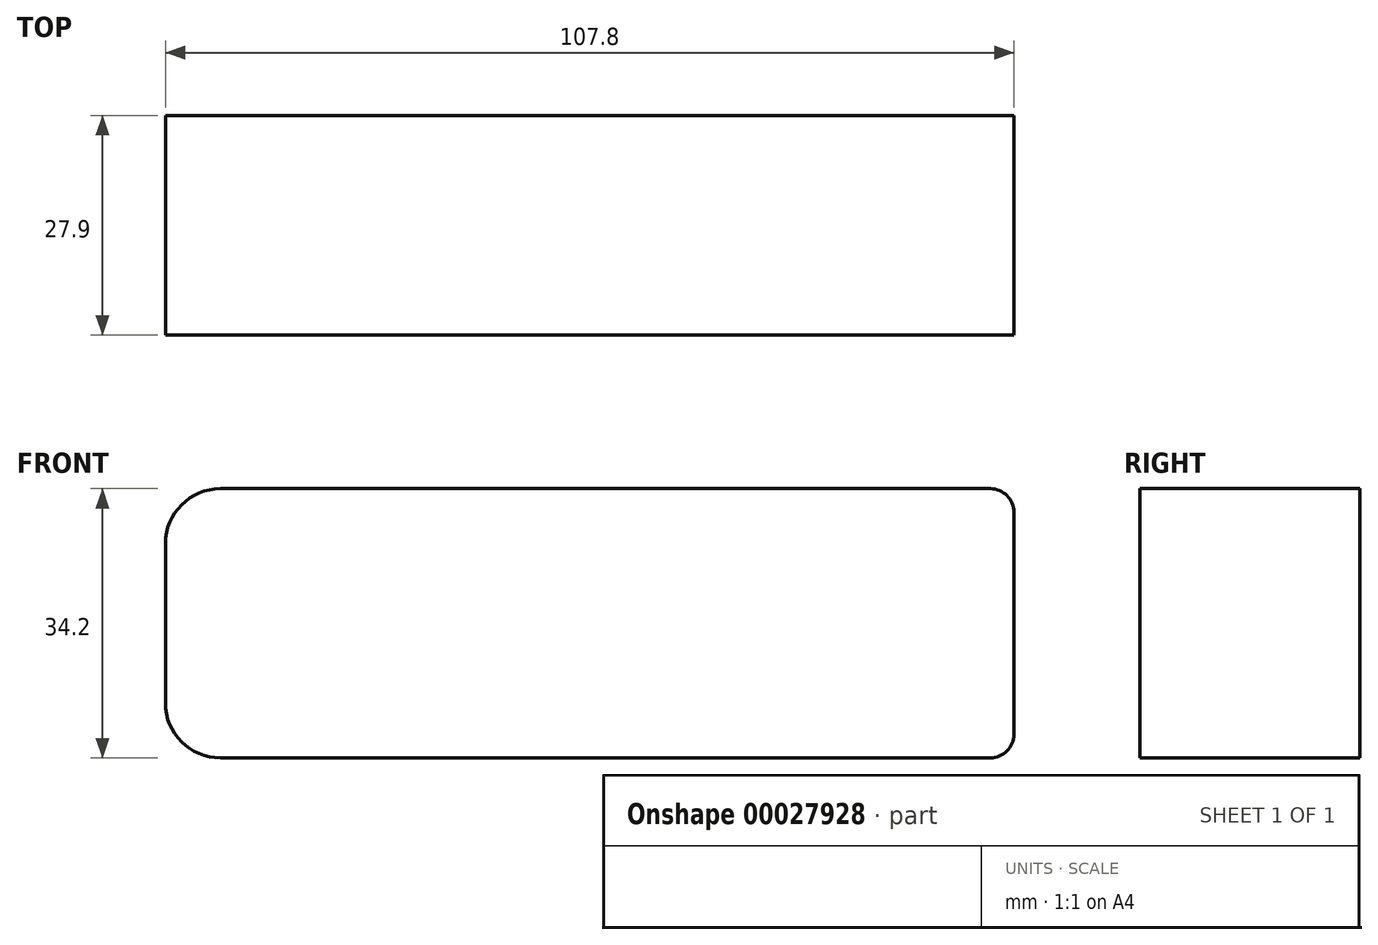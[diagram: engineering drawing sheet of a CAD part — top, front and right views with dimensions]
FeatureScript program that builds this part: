
annotation { "Feature Type Name" : "Feature", "Feature Type Description" : "" }
export const myFeature = defineFeature(function(context is Context, id is Id, definition is map)
    precondition{}
    {
        {
            var Q0;
            Q0=qCreatedBy(makeId("Top.planeOp"),FACE);
            var sketch = newSketch(context, id + "F0", { "sketchPlane" : qUnion([Q0])});
            skLineSegment(sketch, "E0.rect.bottom", {"start": v(53.9, -13.95) * mm, "end": v(-53.9, -13.95) * mm});
            skLineSegment(sketch, "E0.rect.top", {"start": v(53.9, 13.95) * mm, "end": v(-53.9, 13.95) * mm});
            skLineSegment(sketch, "E0.rect.left", {"start": v(53.9, -13.95) * mm, "end": v(53.9, 13.95) * mm});
            skLineSegment(sketch, "E0.rect.right", {"start": v(-53.9, -13.95) * mm, "end": v(-53.9, 13.95) * mm});
            skPoint(sketch, "E0.rect.middle", {"position": v(0, 0) * mm});
            skSolve(sketch);
        }
        {
            var Q0;
            Q0 = qSketchRegion(id + "F0", true);
            extrude(context, id + "F1", {"entities" : qUnion([Q0]), "depth" : 34.2 * mm});
        }
        {
            var Q0;
            Q0=makeQuery(id+"F1.opExtrude","CAP_EDGE",EDGE,{"disambiguationData":[OSD([sQuery(id+"F0.wireOp",EDGE,"E0.rect.right")])],"isStart":false});
            var Q1;
            Q1=makeQuery(id+"F1.opExtrude","CAP_EDGE",EDGE,{"disambiguationData":[OSD([sQuery(id+"F0.wireOp",EDGE,"E0.rect.right")])],"isStart":true});
            fillet(context, id + "F2", {"entities" : qUnion([Q0, Q1]), "radius" : 7 * mm, "tangentPropagation" : true, "allowEdgeOverflow" : false});
        }
        {
            var Q0;
            Q0=makeQuery(id+"F1.opExtrude","CAP_EDGE",EDGE,{"disambiguationData":[OSD([sQuery(id+"F0.wireOp",EDGE,"E0.rect.left")])],"isStart":false});
            var Q1;
            Q1=makeQuery(id+"F1.opExtrude","CAP_EDGE",EDGE,{"disambiguationData":[OSD([sQuery(id+"F0.wireOp",EDGE,"E0.rect.left")])],"isStart":true});
            fillet(context, id + "F3", {"entities" : qUnion([Q0, Q1]), "radius" : 3 * mm, "tangentPropagation" : true, "allowEdgeOverflow" : false});
        }
    });
